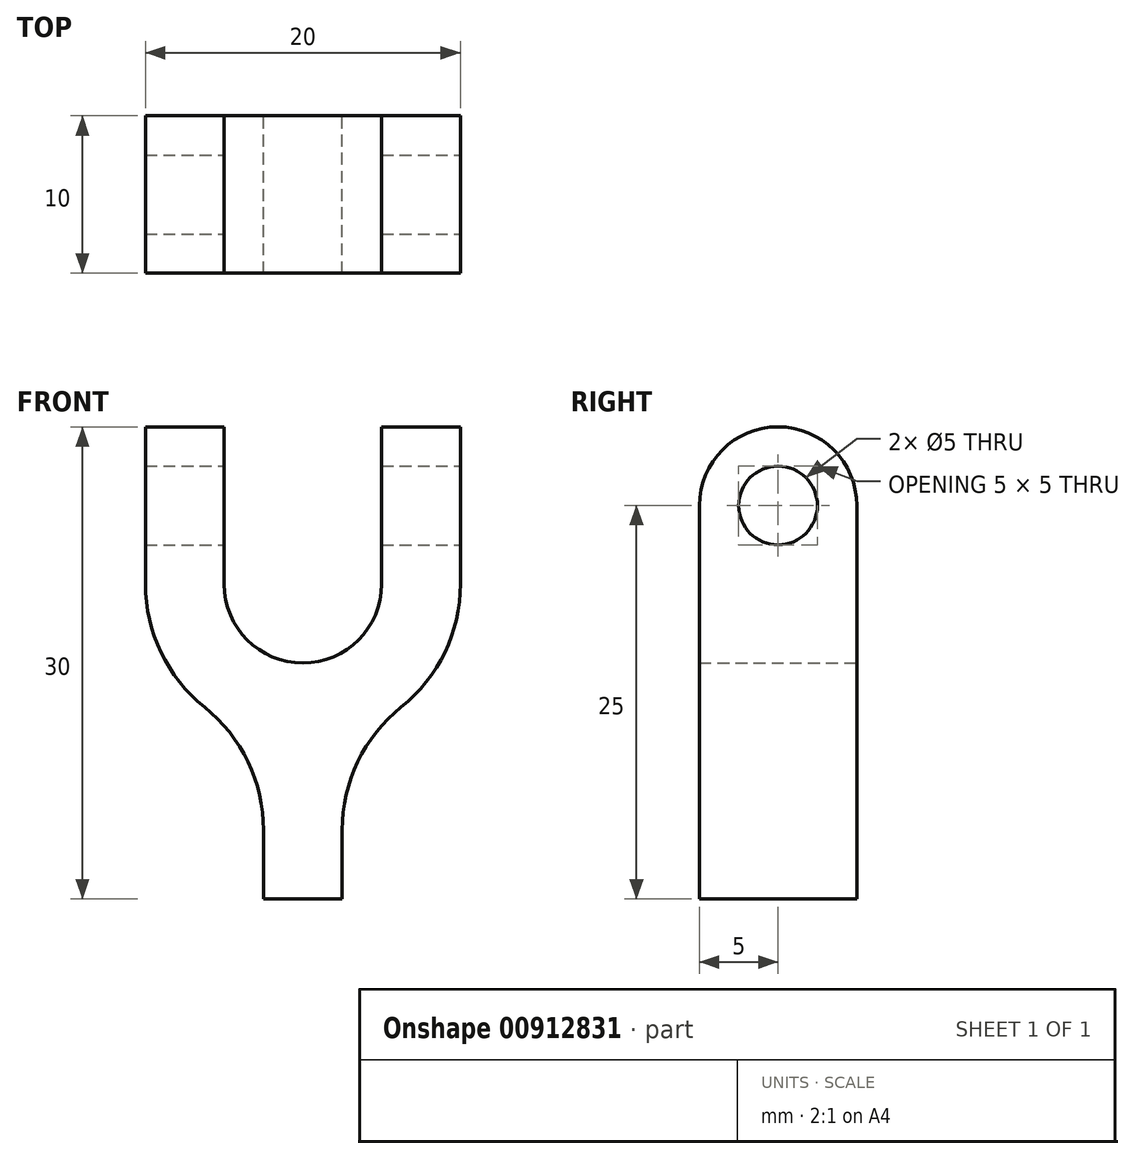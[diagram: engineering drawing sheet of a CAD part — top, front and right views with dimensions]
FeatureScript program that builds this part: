
annotation { "Feature Type Name" : "Feature", "Feature Type Description" : "" }
export const myFeature = defineFeature(function(context is Context, id is Id, definition is map)
    precondition{}
    {
        {
            var Q0;
            Q0=qCreatedBy(makeId("Front.planeOp"),FACE);
            var sketch = newSketch(context, id + "F0", { "sketchPlane" : qUnion([Q0])});
            skLineSegment(sketch, "E0", {"start": v(0, 13.56) * mm, "end": v(0, -13.78) * mm, "construction": true});
            skLineSegment(sketch, "E1", {"start": v(2.5, -15) * mm, "end": v(2.5, -10.61) * mm});
            skArc(sketch, "E2", {"start": v(6.25, -2.8) * mm, "mid": v(3.49, -6.28) * mm, "end": v(2.5, -10.61) * mm});
            skArc(sketch, "E3", {"start": v(6.25, -2.8) * mm, "mid": v(9.01, 0.67) * mm, "end": v(10, 5) * mm});
            skLineSegment(sketch, "E4", {"start": v(10, 5) * mm, "end": v(10, 15) * mm});
            skLineSegment(sketch, "E5", {"start": v(5, 15) * mm, "end": v(5, 5) * mm});
            skArc(sketch, "E6", {"start": v(0, 0) * mm, "mid": v(3.54, 1.46) * mm, "end": v(5, 5) * mm});
            skLineSegment(sketch, "E7", {"start": v(5, 15) * mm, "end": v(10, 15) * mm});
            skLineSegment(sketch, "E8", {"start": v(2.5, -15) * mm, "end": v(0, -15) * mm});
            skArc(sketch, "E9.MirrorCS", {"start": v(-6.25, -2.8) * mm, "mid": v(-3.49, -6.28) * mm, "end": v(-2.5, -10.61) * mm});
            skLineSegment(sketch, "E10.MirrorCS", {"start": v(-2.5, -15) * mm, "end": v(-2.5, -10.61) * mm});
            skLineSegment(sketch, "E11.MirrorCS", {"start": v(-5, 15) * mm, "end": v(-5, 5) * mm});
            skArc(sketch, "E12.MirrorCS", {"start": v(-6.25, -2.8) * mm, "mid": v(-9.01, 0.67) * mm, "end": v(-10, 5) * mm});
            skLineSegment(sketch, "E13.MirrorCS", {"start": v(-2.5, -15) * mm, "end": v(0, -15) * mm});
            skLineSegment(sketch, "E14.MirrorCS", {"start": v(-10, 5) * mm, "end": v(-10, 15) * mm});
            skLineSegment(sketch, "E15.MirrorCS", {"start": v(-5, 15) * mm, "end": v(-10, 15) * mm});
            skArc(sketch, "E16.MirrorCS", {"start": v(0, 0) * mm, "mid": v(-3.54, 1.46) * mm, "end": v(-5, 5) * mm});
            skSolve(sketch);
        }
        {
            var Q0;
            Q0 = qSketchRegion(id + "F0", true);
            extrude(context, id + "F1", {"entities" : qUnion([Q0]), "endBound" : BoundingType.SYMMETRIC, "depth" : 10 * mm, "offsetDistance" : 25 * mm});
        }
        {
            var Q0;
            Q0=makeQuery(id+"F1.opExtrude","CAP_EDGE",EDGE,{"disambiguationData":[OSD([sQuery(id+"F0.wireOp",EDGE,"E15.MirrorCS")])],"isStart":false});
            var Q1;
            Q1=makeQuery(id+"F1.opExtrude","CAP_EDGE",EDGE,{"disambiguationData":[OSD([sQuery(id+"F0.wireOp",EDGE,"E7")])],"isStart":false});
            var Q2;
            Q2=makeQuery(id+"F1.opExtrude","CAP_EDGE",EDGE,{"disambiguationData":[OSD([sQuery(id+"F0.wireOp",EDGE,"E7")])],"isStart":true});
            var Q3;
            Q3=makeQuery(id+"F1.opExtrude","CAP_EDGE",EDGE,{"disambiguationData":[OSD([sQuery(id+"F0.wireOp",EDGE,"E15.MirrorCS")])],"isStart":true});
            fillet(context, id + "F2", {"entities" : qUnion([Q0, Q1, Q2, Q3]), "radius" : 5 * mm, "tangentPropagation" : true, "allowEdgeOverflow" : false});
        }
        {
            var Q0;
            Q0=qCreatedBy(makeId("Right.planeOp"),FACE);
            var sketch = newSketch(context, id + "F3", { "sketchPlane" : qUnion([Q0])});
            skCircle(sketch, "E17", {"center": v(0, 10) * mm, "radius": 2.5 * mm});
            skSolve(sketch);
        }
        {
            var Q0;
            Q0 = qSketchRegion(id + "F3", true);
            extrude(context, id + "F4", {"entities" : qUnion([Q0]), "operationType" : NewBodyOperationType.REMOVE, "endBound" : BoundingType.THROUGH_ALL, "oppositeDirection" : true, "depth" : 25 * mm, "offsetDistance" : 25 * mm, "hasSecondDirection" : true, "secondDirectionBound" : SecondDirectionBoundingType.THROUGH_ALL, "secondDirectionOppositeDirection" : false, "secondDirectionDepth" : 25 * mm});
        }
    });
